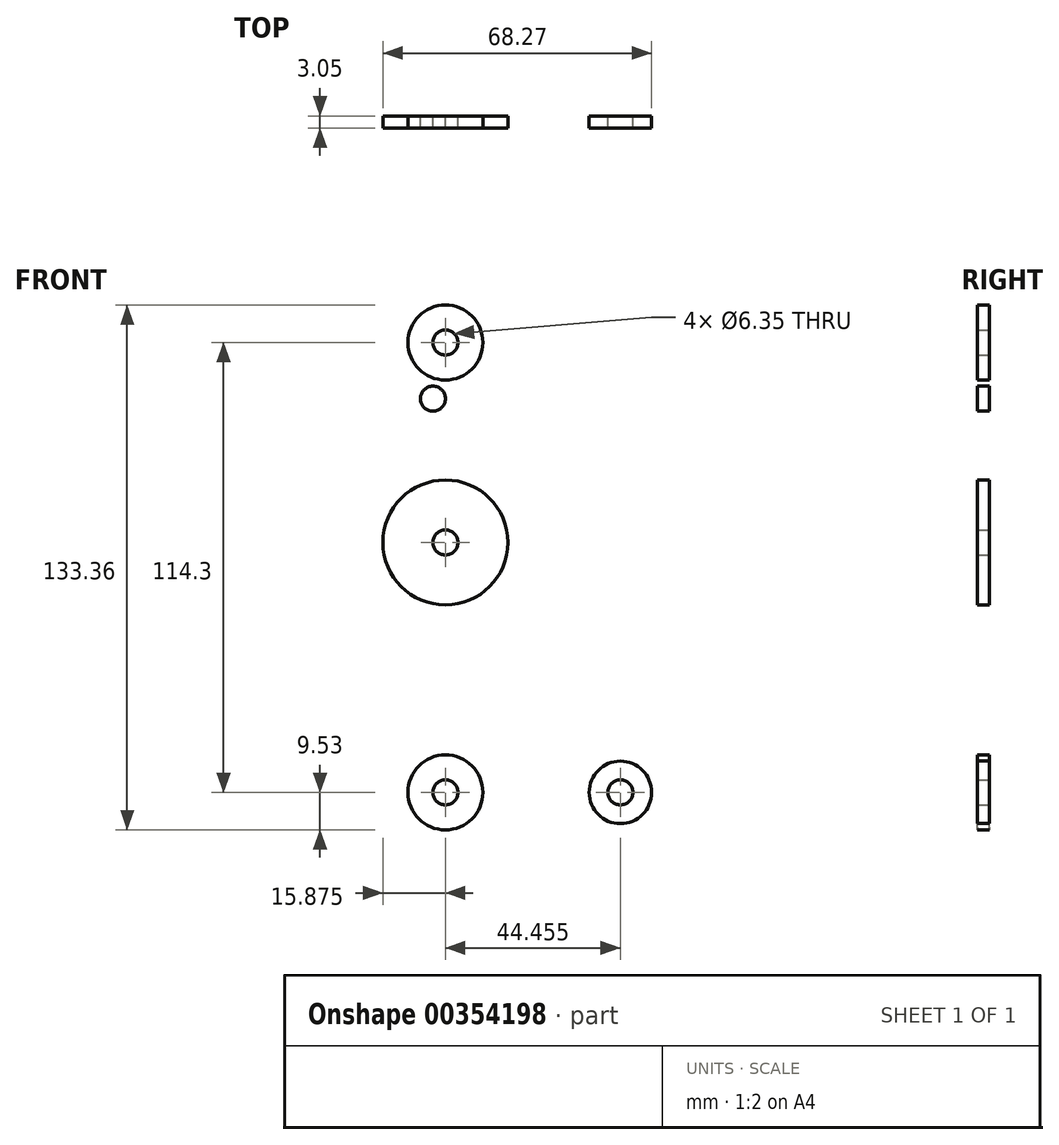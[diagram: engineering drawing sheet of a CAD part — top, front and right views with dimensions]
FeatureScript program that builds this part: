
annotation { "Feature Type Name" : "Feature", "Feature Type Description" : "" }
export const myFeature = defineFeature(function(context is Context, id is Id, definition is map)
    precondition{}
    {
        {
            var Q0;
            Q0=qCreatedBy(makeId("Front.planeOp"),FACE);
            var sketch = newSketch(context, id + "F0", { "sketchPlane" : qUnion([Q0])});
            skLineSegment(sketch, "E0", {"start": v(0, 114.3) * mm, "end": v(0, 0) * mm, "construction": true});
            skCircle(sketch, "E1", {"center": v(0, 63.5) * mm, "radius": 15.88 * mm});
            skCircle(sketch, "E2", {"center": v(0, 114.3) * mm, "radius": 9.53 * mm});
            skCircle(sketch, "E3", {"center": v(0, 0) * mm, "radius": 9.53 * mm});
            skCircle(sketch, "E4", {"center": v(44.45, 0) * mm, "radius": 7.94 * mm});
            skLineSegment(sketch, "E5", {"start": v(18.96, 8.85) * mm, "end": v(44.45, 7.94) * mm});
            skLineSegment(sketch, "E6", {"start": v(0, -9.53) * mm, "end": v(44.73, -7.93) * mm});
            skLineSegment(sketch, "E7", {"start": v(-15.68, 66.04) * mm, "end": v(-9.45, 115.49) * mm});
            skLineSegment(sketch, "E8", {"start": v(15.67, 61) * mm, "end": v(11.33, 17.59) * mm});
            skLineSegment(sketch, "E9", {"start": v(-15.68, 61) * mm, "end": v(-9.48, -0.95) * mm});
            skLineSegment(sketch, "E10", {"start": v(9.45, 115.49) * mm, "end": v(15.68, 66.04) * mm});
            skLineSegment(sketch, "E11", {"start": v(0, 0) * mm, "end": v(44.45, 0) * mm, "construction": true});
            skCircle(sketch, "E12", {"center": v(-3.18, 100.03) * mm, "radius": 3.18 * mm});
            skCircle(sketch, "E13", {"center": v(0, 114.3) * mm, "radius": 3.18 * mm});
            skCircle(sketch, "E14", {"center": v(0, 63.5) * mm, "radius": 3.18 * mm});
            skCircle(sketch, "E15", {"center": v(0, 0) * mm, "radius": 3.18 * mm});
            skCircle(sketch, "E16", {"center": v(44.45, 0) * mm, "radius": 3.18 * mm});
            skPoint(sketch, "E17.newPointA", {"position": v(9.48, -0.95) * mm});
            skArc(sketch, "E17.filletArc", {"start": v(11.33, 17.59) * mm, "mid": v(13.25, 11.57) * mm, "end": v(18.96, 8.85) * mm});
            skSolve(sketch);
        }
        {
            var Q0;
            Q0 = qSketchRegion(id + "F0", true);
            extrude(context, id + "F1", {"entities" : qUnion([Q0]), "depth" : 3.05 * mm});
        }
    });
